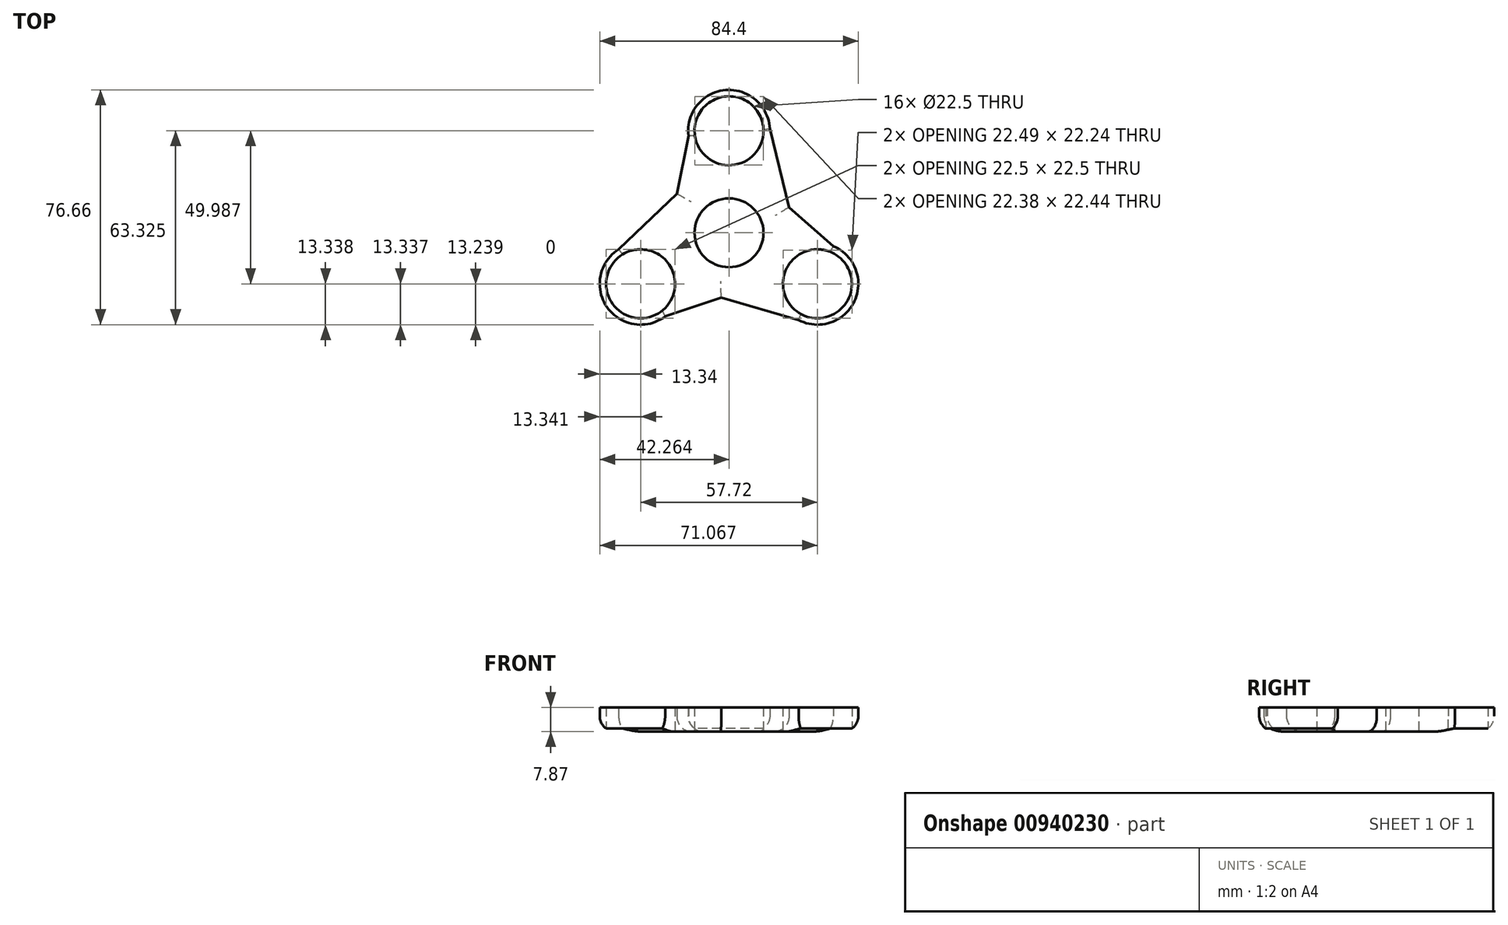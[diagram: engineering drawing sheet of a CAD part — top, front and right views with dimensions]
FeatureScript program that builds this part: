
annotation { "Feature Type Name" : "Feature", "Feature Type Description" : "" }
export const myFeature = defineFeature(function(context is Context, id is Id, definition is map)
    precondition{}
    {
        {
            var Q0;
            Q0=qCreatedBy(makeId("Top.planeOp"),FACE);
            var sketch = newSketch(context, id + "F0", { "sketchPlane" : qUnion([Q0])});
            skCircle(sketch, "E0", {"center": v(0, 0) * mm, "radius": 11.25 * mm});
            skCircle(sketch, "E1", {"center": v(0, 33.32) * mm, "radius": 11.25 * mm});
            skArc(sketch, "E2", {"start": v(13.32, 33.9) * mm, "mid": v(-1.1, 46.61) * mm, "end": v(-13.24, 31.7) * mm});
            skLineSegment(sketch, "E3", {"start": v(-13.24, 31.7) * mm, "end": v(-17.04, 12.78) * mm});
            skLineSegment(sketch, "E4", {"start": v(19.59, 8.37) * mm, "end": v(13.32, 33.9) * mm});
            skLineSegment(sketch, "E5.1.0", {"start": v(-20.84, -27.31) * mm, "end": v(-2.55, -21.15) * mm});
            skLineSegment(sketch, "E5.1.1", {"start": v(-17.04, 12.78) * mm, "end": v(-36.02, -5.41) * mm});
            skCircle(sketch, "E5.1.2", {"center": v(-28.86, -16.66) * mm, "radius": 11.25 * mm});
            skArc(sketch, "E5.1.3", {"start": v(-36.02, -5.41) * mm, "mid": v(-39.82, -24.26) * mm, "end": v(-20.84, -27.31) * mm});
            skLineSegment(sketch, "E5.2.0", {"start": v(34.07, -4.39) * mm, "end": v(19.59, 8.37) * mm});
            skLineSegment(sketch, "E5.2.1", {"start": v(-2.55, -21.15) * mm, "end": v(22.7, -28.49) * mm});
            skCircle(sketch, "E5.2.2", {"center": v(28.86, -16.66) * mm, "radius": 11.25 * mm});
            skArc(sketch, "E5.2.3", {"start": v(22.7, -28.49) * mm, "mid": v(40.92, -22.35) * mm, "end": v(34.07, -4.39) * mm});
            skSolve(sketch);
        }
        {
            var Q0;
            Q0 = qSketchRegion(id + "F0", true);
            extrude(context, id + "F1", {"entities" : qUnion([Q0]), "depth" : 7.87 * mm, "offsetDistance" : 25.4 * mm});
        }
        {
            var Q0;
            Q0=makeQuery(id+"F1.opExtrude","CAP_EDGE",EDGE,{"disambiguationData":[OSD([sQuery(id+"F0.wireOp",EDGE,"E5.1.0")])],"isStart":true});
            var Q1;
            Q1=makeQuery(id+"F1.opExtrude","CAP_EDGE",EDGE,{"disambiguationData":[OSD([sQuery(id+"F0.wireOp",EDGE,"E5.2.1")])],"isStart":true});
            var Q2;
            Q2=makeQuery(id+"F1.opExtrude","CAP_EDGE",EDGE,{"disambiguationData":[OSD([sQuery(id+"F0.wireOp",EDGE,"E5.2.0")])],"isStart":true});
            var Q3;
            Q3=makeQuery(id+"F1.opExtrude","CAP_EDGE",EDGE,{"disambiguationData":[OSD([sQuery(id+"F0.wireOp",EDGE,"E4")])],"isStart":true});
            var Q4;
            Q4=makeQuery(id+"F1.opExtrude","CAP_EDGE",EDGE,{"disambiguationData":[OSD([sQuery(id+"F0.wireOp",EDGE,"E3")])],"isStart":true});
            var Q5;
            Q5=makeQuery(id+"F1.opExtrude","CAP_EDGE",EDGE,{"disambiguationData":[OSD([sQuery(id+"F0.wireOp",EDGE,"E5.1.1")])],"isStart":true});
            var Q6;
            Q6=makeQuery(id+"F1.opExtrude","CAP_EDGE",EDGE,{"disambiguationData":[OSD([sQuery(id+"F0.wireOp",EDGE,"E5.1.3")])],"isStart":true});
            var Q7;
            Q7=makeQuery(id+"F1.opExtrude","CAP_EDGE",EDGE,{"disambiguationData":[OSD([sQuery(id+"F0.wireOp",EDGE,"E5.2.3")])],"isStart":true});
            var Q8;
            Q8=makeQuery(id+"F1.opExtrude","CAP_EDGE",EDGE,{"disambiguationData":[OSD([sQuery(id+"F0.wireOp",EDGE,"E2")])],"isStart":true});
            fillet(context, id + "F2", {"entities" : qUnion([Q0, Q1, Q2, Q3, Q4, Q5, Q6, Q7, Q8]), "radius" : 5.08 * mm, "tangentPropagation" : true, "allowEdgeOverflow" : false});
        }
    });
